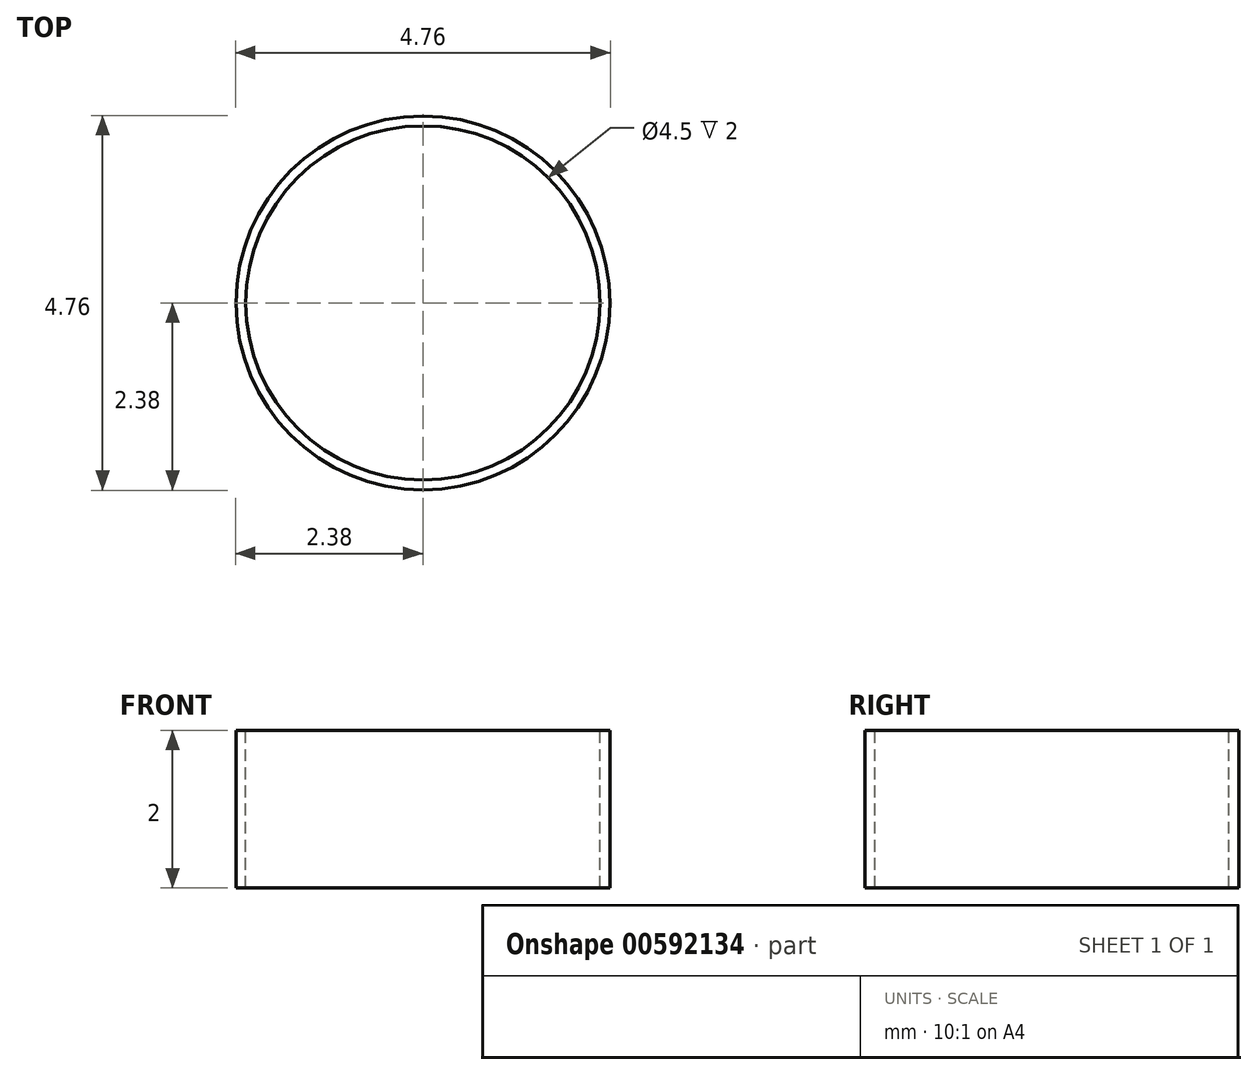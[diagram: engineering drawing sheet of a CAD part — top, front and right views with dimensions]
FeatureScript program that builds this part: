
annotation { "Feature Type Name" : "Feature", "Feature Type Description" : "" }
export const myFeature = defineFeature(function(context is Context, id is Id, definition is map)
    precondition{}
    {
        {
            var Q0;
            Q0=qCreatedBy(makeId("Top.planeOp"),FACE);
            var sketch = newSketch(context, id + "F0", { "sketchPlane" : qUnion([Q0])});
            skCircle(sketch, "E0", {"center": v(0, 0) * mm, "radius": 4.75 * mm});
            skSolve(sketch);
        }
        {
            var Q0;
            Q0 = qSketchRegion(id + "F0", true);
            extrude(context, id + "F1", {"entities" : qUnion([Q0]), "depth" : 4 * mm, "offsetDistance" : 25 * mm});
        }
        {
            var Q0;
            Q0=makeQuery(id+"F1.opExtrude","SWEPT_BODY",BODY,{"disambiguationData":[OSD([sQuery(id+"F0.wireOp",EDGE,"E0")])]});
            var Q1;
            Q1=qCreatedBy(makeId("Origin.pointOp"),VERTEX);
            transform(context, id + "F2", {"entities" : qUnion([Q0]), "transformType" : TransformType.SCALE_UNIFORMLY, "scale" : .5, "scalePoint" : qUnion([Q1]), "makeCopy" : false});
        }
        {
            var Q0;
            Q0=makeQuery(id+"F1.opExtrude","CAP_FACE",FACE,{"disambiguationData":[OSD([sQuery(id+"F0.wireOp",EDGE,"E0")])],"isStart":false});
            var sketch = newSketch(context, id + "F3", { "sketchPlane" : qUnion([Q0])});
            skCircle(sketch, "E1", {"center": v(0, 0) * mm, "radius": 2.25 * mm});
            skSolve(sketch);
        }
        {
            var Q0;
            Q0 = qSketchRegion(id + "F3", true);
            extrude(context, id + "F4", {"entities" : qUnion([Q0]), "operationType" : NewBodyOperationType.REMOVE, "oppositeDirection" : true, "depth" : 25 * mm, "offsetDistance" : 25 * mm});
        }
    });
